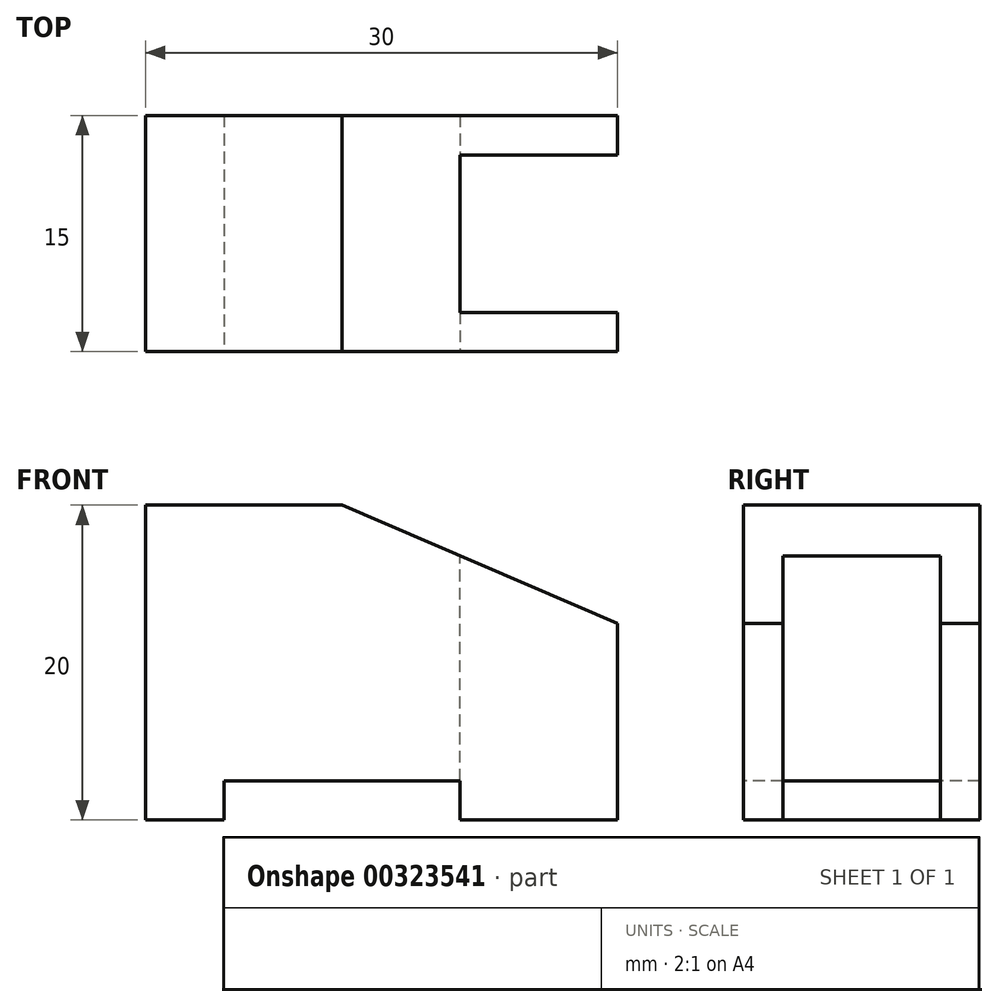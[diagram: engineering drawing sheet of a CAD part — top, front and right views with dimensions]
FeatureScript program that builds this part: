
annotation { "Feature Type Name" : "Feature", "Feature Type Description" : "" }
export const myFeature = defineFeature(function(context is Context, id is Id, definition is map)
    precondition{}
    {
        {
            var Q0;
            Q0=qCreatedBy(makeId("Front.planeOp"),FACE);
            var sketch = newSketch(context, id + "F0", { "sketchPlane" : qUnion([Q0])});
            skLineSegment(sketch, "E0", {"start": v(0, 0) * mm, "end": v(0, 20) * mm});
            skLineSegment(sketch, "E1", {"start": v(0, 20) * mm, "end": v(12.5, 20) * mm});
            skLineSegment(sketch, "E2", {"start": v(12.5, 20) * mm, "end": v(30, 12.5) * mm});
            skLineSegment(sketch, "E3", {"start": v(30, 12.5) * mm, "end": v(30, 0) * mm});
            skLineSegment(sketch, "E4", {"start": v(30, 0) * mm, "end": v(20, 0) * mm});
            skLineSegment(sketch, "E5", {"start": v(20, 0) * mm, "end": v(20, 2.5) * mm});
            skLineSegment(sketch, "E6", {"start": v(20, 2.5) * mm, "end": v(5, 2.5) * mm});
            skLineSegment(sketch, "E7", {"start": v(5, 2.5) * mm, "end": v(5, 0) * mm});
            skLineSegment(sketch, "E8", {"start": v(5, 0) * mm, "end": v(0, 0) * mm});
            skLineSegment(sketch, "E9", {"start": v(12.5, 20) * mm, "end": v(30, 20) * mm});
            skLineSegment(sketch, "E10", {"start": v(30, 20) * mm, "end": v(30, 12.5) * mm});
            skSolve(sketch);
        }
        {
            var Q0;
            Q0=makeQuery(id+"F0.imprint","IMPRINT",FACE,{"disambiguationData":[TD([[makeQuery(id+"F0.imprint","IMPRINT",EDGE,{"derivedFrom":sQuery(id+"F0.wireOp",EDGE,"E0")}),-1.0]])]});
            extrude(context, id + "F1", {"entities" : qUnion([Q0]), "oppositeDirection" : true, "depth" : 15 * mm});
        }
        {
            var Q0;
            Q0=makeQuery(id+"F0.imprint","IMPRINT",FACE,{"disambiguationData":[TD([[makeQuery(id+"F0.imprint","IMPRINT",EDGE,{"derivedFrom":sQuery(id+"F0.wireOp",EDGE,"E2")}),1.0]])]});
            extrude(context, id + "F2", {"entities" : qUnion([Q0]), "operationType" : NewBodyOperationType.ADD, "oppositeDirection" : true, "depth" : 15 * mm});
        }
        {
            var Q0;
            Q0=makeQuery(id+"F2.boolean.opBoolean","MERGE",FACE,{"derivedFrom":[makeQuery(id+"F1.opExtrude","SWEPT_FACE",FACE,{"disambiguationData":[OSD([sQuery(id+"F0.wireOp",EDGE,"E1")])]}),makeQuery(id+"F2.opExtrude","SWEPT_FACE",FACE,{"disambiguationData":[OSD([sQuery(id+"F0.wireOp",EDGE,"E9")])]})]});
            var sketch = newSketch(context, id + "F3", { "sketchPlane" : qUnion([Q0])});
            skLineSegment(sketch, "E11.bottom", {"start": v(20, 12.5) * mm, "end": v(30, 12.5) * mm});
            skLineSegment(sketch, "E11.top", {"start": v(20, 2.5) * mm, "end": v(30, 2.5) * mm});
            skLineSegment(sketch, "E11.left", {"start": v(20, 12.5) * mm, "end": v(20, 2.5) * mm});
            skLineSegment(sketch, "E11.right", {"start": v(30, 12.5) * mm, "end": v(30, 2.5) * mm});
            skSolve(sketch);
        }
        {
            var Q0;
            Q0=makeQuery(id+"F3.imprint","IMPRINT",FACE,{"disambiguationData":[TD([[makeQuery(id+"F3.imprint","IMPRINT",EDGE,{"derivedFrom":sQuery(id+"F3.wireOp",EDGE,"E11.bottom")}),-1.0]])]});
            extrude(context, id + "F4", {"entities" : qUnion([Q0]), "operationType" : NewBodyOperationType.REMOVE, "endBound" : BoundingType.THROUGH_ALL, "oppositeDirection" : true, "depth" : 25 * mm});
        }
        {
            var Q0;
            Q0=makeQuery(id+"F0.imprint","IMPRINT",FACE,{"disambiguationData":[TD([[makeQuery(id+"F0.imprint","IMPRINT",EDGE,{"derivedFrom":sQuery(id+"F0.wireOp",EDGE,"E2")}),1.0]])]});
            extrude(context, id + "F5", {"entities" : qUnion([Q0]), "operationType" : NewBodyOperationType.REMOVE, "endBound" : BoundingType.THROUGH_ALL, "oppositeDirection" : true, "depth" : 25 * mm});
        }
    });
